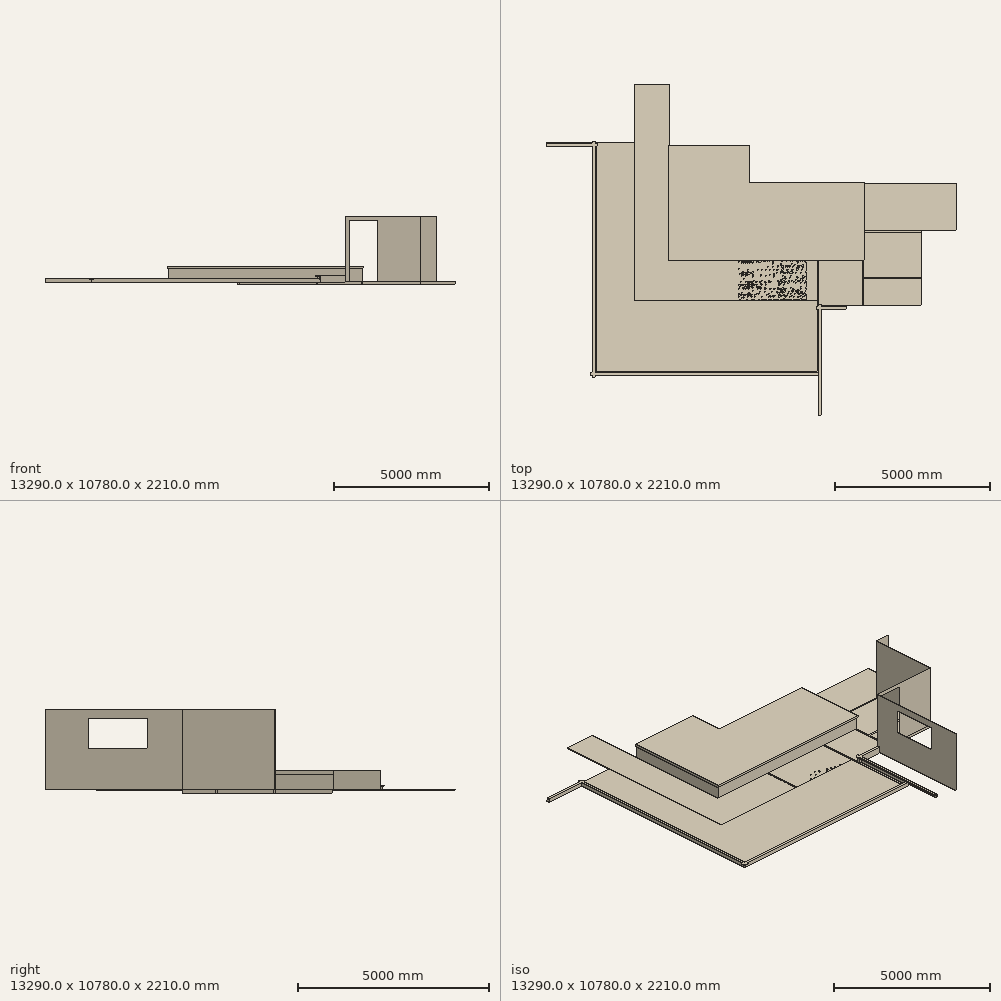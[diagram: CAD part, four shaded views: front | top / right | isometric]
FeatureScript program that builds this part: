
annotation { "Feature Type Name" : "Feature", "Feature Type Description" : "" }
export const myFeature = defineFeature(function(context is Context, id is Id, definition is map)
    precondition{}
    {
        {
            var Q0;
            Q0=qCreatedBy(makeId("Top.planeOp"),FACE);
            var sketch = newSketch(context, id + "F0", { "sketchPlane" : qUnion([Q0])});
            skLineSegment(sketch, "E0", {"start": v(0, 0) * mm, "end": v(0, 1220) * mm});
            skLineSegment(sketch, "E1", {"start": v(0, 1220) * mm, "end": v(-2595, 1220) * mm});
            skLineSegment(sketch, "E2", {"start": v(-2595, 1220) * mm, "end": v(-2595, -2530) * mm});
            skLineSegment(sketch, "E3", {"start": v(-2595, -2530) * mm, "end": v(3755, -2530) * mm});
            skLineSegment(sketch, "E4", {"start": v(3755, -2530) * mm, "end": v(3755, 0) * mm});
            skLineSegment(sketch, "E5", {"start": v(3755, 0) * mm, "end": v(0, 0) * mm});
            skSolve(sketch);
        }
        {
            var Q0;
            Q0 = qSketchRegion(id + "F0", true);
            extrude(context, id + "F1", {"entities" : qUnion([Q0]), "oppositeDirection" : true, "depth" : 85 * mm});
        }
        {
            var Q0;
            Q0=makeQuery(id+"F1.opExtrude","CAP_FACE",FACE,{"disambiguationData":[OSD([sQuery(id+"F0.wireOp",EDGE,"E0"),sQuery(id+"F0.wireOp",EDGE,"E1"),sQuery(id+"F0.wireOp",EDGE,"E2"),sQuery(id+"F0.wireOp",EDGE,"E3"),sQuery(id+"F0.wireOp",EDGE,"E4"),sQuery(id+"F0.wireOp",EDGE,"E5")])],"isStart":false});
            var sketch = newSketch(context, id + "F2", { "sketchPlane" : qUnion([Q0])});
            skLineSegment(sketch, "E6", {"start": v(-2565, -1220) * mm, "end": v(-2565, 2500) * mm});
            skLineSegment(sketch, "E7", {"start": v(-2565, 2500) * mm, "end": v(3725, 2500) * mm});
            skLineSegment(sketch, "E8", {"start": v(3725, 2500) * mm, "end": v(3725, 0) * mm});
            skLineSegment(sketch, "E9", {"start": v(3725, 0) * mm, "end": v(0, 0) * mm});
            skLineSegment(sketch, "E10", {"start": v(0, 0) * mm, "end": v(0, -1220) * mm});
            skLineSegment(sketch, "E11", {"start": v(0, -1220) * mm, "end": v(-2565, -1220) * mm});
            skSolve(sketch);
        }
        {
            var Q0;
            Q0 = qSketchRegion(id + "F2", true);
            extrude(context, id + "F3", {"entities" : qUnion([Q0]), "operationType" : NewBodyOperationType.ADD, "depth" : 410 * mm});
        }
        {
            var Q0;
            Q0=makeQuery(id+"F3.opExtrude","CAP_FACE",FACE,{"disambiguationData":[OSD([sQuery(id+"F2.wireOp",EDGE,"E6"),sQuery(id+"F2.wireOp",EDGE,"E7"),sQuery(id+"F2.wireOp",EDGE,"E8"),sQuery(id+"F2.wireOp",EDGE,"E9"),sQuery(id+"F2.wireOp",EDGE,"E10"),sQuery(id+"F2.wireOp",EDGE,"E11")])],"isStart":false});
            var sketch = newSketch(context, id + "F4", { "sketchPlane" : qUnion([Q0])});
            skLineSegment(sketch, "E12", {"start": v(-2565, 2500) * mm, "end": v(1875, 2500) * mm});
            skLineSegment(sketch, "E13", {"start": v(1875, 2500) * mm, "end": v(1875, 3800) * mm});
            skLineSegment(sketch, "E14", {"start": v(1875, 3800) * mm, "end": v(-3705, 3800) * mm});
            skLineSegment(sketch, "E15", {"start": v(-3705, 3800) * mm, "end": v(-3705, -3200) * mm});
            skLineSegment(sketch, "E16", {"start": v(-3705, -3200) * mm, "end": v(-2565, -3200) * mm});
            skLineSegment(sketch, "E17", {"start": v(-2565, -3200) * mm, "end": v(-2565, 2500) * mm});
            skSolve(sketch);
        }
        {
            var Q0;
            Q0 = qSketchRegion(id + "F4", true);
            extrude(context, id + "F5", {"entities" : qUnion([Q0]), "depth" : 25 * mm});
        }
        {
            var Q0;
            Q0=makeQuery(id+"F5.opExtrude","CAP_FACE",FACE,{"disambiguationData":[OSD([sQuery(id+"F4.wireOp",EDGE,"E12"),sQuery(id+"F4.wireOp",EDGE,"E13"),sQuery(id+"F4.wireOp",EDGE,"E14"),sQuery(id+"F4.wireOp",EDGE,"E15"),sQuery(id+"F4.wireOp",EDGE,"E16"),sQuery(id+"F4.wireOp",EDGE,"E17")])],"isStart":true});
            var sketch = newSketch(context, id + "F6", { "sketchPlane" : qUnion([Q0])});
            skLineSegment(sketch, "E18", {"start": v(2215, -3980) * mm, "end": v(3165, -3980) * mm});
            skLineSegment(sketch, "E19", {"start": v(2215, -3980) * mm, "end": v(2215, -6110) * mm});
            skLineSegment(sketch, "E20", {"start": v(2215, -6110) * mm, "end": v(-4960, -6110) * mm});
            skLineSegment(sketch, "E21", {"start": v(-4960, -6110) * mm, "end": v(-4960, 1295) * mm});
            skLineSegment(sketch, "E22", {"start": v(-4960, 1295) * mm, "end": v(-6565, 1295) * mm});
            skLineSegment(sketch, "E23", {"start": v(-6565, 1295) * mm, "end": v(-6565, 1170) * mm});
            skLineSegment(sketch, "E24", {"start": v(-6565, 1170) * mm, "end": v(-5085, 1170) * mm});
            skLineSegment(sketch, "E25", {"start": v(-5085, 1170) * mm, "end": v(-5085, -6235) * mm});
            skLineSegment(sketch, "E26", {"start": v(-5085, -6235) * mm, "end": v(2340, -6235) * mm});
            skLineSegment(sketch, "E27", {"start": v(2340, -6235) * mm, "end": v(2340, -4105) * mm});
            skLineSegment(sketch, "E28", {"start": v(2340, -4105) * mm, "end": v(3165, -4105) * mm});
            skLineSegment(sketch, "E29", {"start": v(3165, -4105) * mm, "end": v(3165, -3980) * mm});
            skSolve(sketch);
        }
        {
            var Q0;
            Q0=makeQuery(id+"F6.imprint","IMPRINT",FACE,{"disambiguationData":[TD([[makeQuery(id+"F6.imprint","IMPRINT",EDGE,{"derivedFrom":sQuery(id+"F6.wireOp",EDGE,"E18")}),-1.0]])]});
            extrude(context, id + "F7", {"entities" : qUnion([Q0]), "oppositeDirection" : true, "offsetDistance" : 25 * mm, "depth" : 25 * mm});
        }
        {
            var Q0;
            Q0=makeQuery(id+"F7.opExtrude","CAP_FACE",FACE,{"disambiguationData":[OSD([sQuery(id+"F6.wireOp",EDGE,"E18"),sQuery(id+"F6.wireOp",EDGE,"E19"),sQuery(id+"F6.wireOp",EDGE,"E20"),sQuery(id+"F6.wireOp",EDGE,"E21"),sQuery(id+"F6.wireOp",EDGE,"E22"),sQuery(id+"F6.wireOp",EDGE,"E23"),sQuery(id+"F6.wireOp",EDGE,"E24"),sQuery(id+"F6.wireOp",EDGE,"E25"),sQuery(id+"F6.wireOp",EDGE,"E26"),sQuery(id+"F6.wireOp",EDGE,"E27"),sQuery(id+"F6.wireOp",EDGE,"E28"),sQuery(id+"F6.wireOp",EDGE,"E29")])],"isStart":true});
            var sketch = newSketch(context, id + "F8", { "sketchPlane" : qUnion([Q0])});
            skLineSegment(sketch, "E30", {"start": v(3140, -4005) * mm, "end": v(3140, -4080) * mm});
            skLineSegment(sketch, "E31", {"start": v(3140, -4080) * mm, "end": v(2340, -4080) * mm});
            skLineSegment(sketch, "E32", {"start": v(2315, -4105) * mm, "end": v(2315, -6135) * mm});
            skLineSegment(sketch, "E33", {"start": v(2315, -6135) * mm, "end": v(2240, -6135) * mm});
            skLineSegment(sketch, "E34", {"start": v(2240, -6135) * mm, "end": v(2240, -6210) * mm});
            skLineSegment(sketch, "E35", {"start": v(2240, -6210) * mm, "end": v(508.75, -6210) * mm});
            skLineSegment(sketch, "E36", {"start": v(-4985, -6210) * mm, "end": v(-4985, -6135) * mm});
            skLineSegment(sketch, "E37", {"start": v(-4985, -6135) * mm, "end": v(-5060, -6135) * mm});
            skLineSegment(sketch, "E38", {"start": v(-5060, -6135) * mm, "end": v(-5060, -4383.75) * mm});
            skLineSegment(sketch, "E39", {"start": v(-5060, 1170) * mm, "end": v(-4985, 1170) * mm});
            skLineSegment(sketch, "E40", {"start": v(-4985, 1170) * mm, "end": v(-4985, 1270) * mm});
            skLineSegment(sketch, "E41", {"start": v(-4985, 1270) * mm, "end": v(-5085, 1270) * mm});
            skLineSegment(sketch, "E42", {"start": v(-5085, 1270) * mm, "end": v(-5085, 1195) * mm});
            skLineSegment(sketch, "E43", {"start": v(-5085, 1195) * mm, "end": v(-6540, 1195) * mm});
            skLineSegment(sketch, "E44", {"start": v(-6540, 1195) * mm, "end": v(-6540, 1270) * mm});
            skLineSegment(sketch, "E45", {"start": v(-6540, 1270) * mm, "end": v(-6565, 1270) * mm});
            skLineSegment(sketch, "E46", {"start": v(-6565, 1270) * mm, "end": v(-6565, 1170) * mm});
            skLineSegment(sketch, "E47", {"start": v(-6565, 1170) * mm, "end": v(-5085, 1170) * mm});
            skLineSegment(sketch, "E48", {"start": v(-5085, 1170) * mm, "end": v(-5085, -6235) * mm});
            skLineSegment(sketch, "E49", {"start": v(-5085, -6235) * mm, "end": v(2340, -6235) * mm});
            skLineSegment(sketch, "E50", {"start": v(2340, -6235) * mm, "end": v(2340, -4105) * mm});
            skLineSegment(sketch, "E51", {"start": v(2340, -4105) * mm, "end": v(3165, -4105) * mm});
            skLineSegment(sketch, "E52", {"start": v(3165, -4105) * mm, "end": v(3165, -4005) * mm});
            skLineSegment(sketch, "E53", {"start": v(3165, -4005) * mm, "end": v(3140, -4005) * mm});
            skLineSegment(sketch, "E54", {"start": v(2340, -4080) * mm, "end": v(2340, -4005) * mm});
            skLineSegment(sketch, "E55", {"start": v(2340, -4005) * mm, "end": v(2240, -4005) * mm});
            skLineSegment(sketch, "E56", {"start": v(2240, -4005) * mm, "end": v(2240, -4105) * mm});
            skLineSegment(sketch, "E57", {"start": v(2240, -4105) * mm, "end": v(2315, -4105) * mm});
            skLineSegment(sketch, "E58", {"start": v(-1422.5, -6210) * mm, "end": v(-1422.5, -6135) * mm});
            skLineSegment(sketch, "E59", {"start": v(-1422.5, -6135) * mm, "end": v(-1322.5, -6135) * mm});
            skLineSegment(sketch, "E60", {"start": v(-1322.5, -6135) * mm, "end": v(-1322.5, -6210) * mm});
            skLineSegment(sketch, "E61", {"start": v(-3253.75, -6210) * mm, "end": v(-3253.75, -6135) * mm});
            skLineSegment(sketch, "E62", {"start": v(-3253.75, -6135) * mm, "end": v(-3153.75, -6135) * mm});
            skLineSegment(sketch, "E63", {"start": v(-3153.75, -6135) * mm, "end": v(-3153.75, -6210) * mm});
            skLineSegment(sketch, "E64", {"start": v(408.75, -6210) * mm, "end": v(408.75, -6135) * mm});
            skLineSegment(sketch, "E65", {"start": v(408.75, -6135) * mm, "end": v(508.75, -6135) * mm});
            skLineSegment(sketch, "E66", {"start": v(508.75, -6135) * mm, "end": v(508.75, -6210) * mm});
            skLineSegment(sketch, "E67.trimOffspring", {"start": v(-3253.75, -6210) * mm, "end": v(-4985, -6210) * mm});
            skLineSegment(sketch, "E68.trimOffspring", {"start": v(-1422.5, -6210) * mm, "end": v(-3153.75, -6210) * mm});
            skLineSegment(sketch, "E69.trimOffspring", {"start": v(408.75, -6210) * mm, "end": v(-1322.5, -6210) * mm});
            skLineSegment(sketch, "E70", {"start": v(-5060, -4383.75) * mm, "end": v(-4985, -4383.75) * mm});
            skLineSegment(sketch, "E71", {"start": v(-4985, -4383.75) * mm, "end": v(-4985, -4283.75) * mm});
            skLineSegment(sketch, "E72", {"start": v(-4985, -4283.75) * mm, "end": v(-5060, -4283.75) * mm});
            skLineSegment(sketch, "E73", {"start": v(-5060, -2532.5) * mm, "end": v(-4985, -2532.5) * mm});
            skLineSegment(sketch, "E74", {"start": v(-4985, -2532.5) * mm, "end": v(-4985, -2432.5) * mm});
            skLineSegment(sketch, "E75", {"start": v(-4985, -2432.5) * mm, "end": v(-5060, -2432.5) * mm});
            skLineSegment(sketch, "E76", {"start": v(-5060, -681.25) * mm, "end": v(-4985, -681.25) * mm});
            skLineSegment(sketch, "E77", {"start": v(-4985, -681.25) * mm, "end": v(-4985, -581.25) * mm});
            skLineSegment(sketch, "E78", {"start": v(-4985, -581.25) * mm, "end": v(-5060, -581.25) * mm});
            skLineSegment(sketch, "E79.trimOffspring", {"start": v(-5060, -581.25) * mm, "end": v(-5060, 1170) * mm});
            skLineSegment(sketch, "E80.trimOffspring", {"start": v(-5060, -2432.5) * mm, "end": v(-5060, -681.25) * mm});
            skLineSegment(sketch, "E81.trimOffspring", {"start": v(-5060, -4283.75) * mm, "end": v(-5060, -2532.5) * mm});
            skSolve(sketch);
        }
        {
            var Q0;
            Q0 = qSketchRegion(id + "F8", true);
            extrude(context, id + "F9", {"entities" : qUnion([Q0]), "operationType" : NewBodyOperationType.ADD, "depth" : 75 * mm});
        }
        {
            var Q0;
            Q0=makeQuery(id+"F9.opExtrude","CAP_FACE",FACE,{"disambiguationData":[OSD([sQuery(id+"F8.wireOp",EDGE,"E30"),sQuery(id+"F8.wireOp",EDGE,"E31"),sQuery(id+"F8.wireOp",EDGE,"E32"),sQuery(id+"F8.wireOp",EDGE,"E33"),sQuery(id+"F8.wireOp",EDGE,"E34"),sQuery(id+"F8.wireOp",EDGE,"E35"),sQuery(id+"F8.wireOp",EDGE,"E36"),sQuery(id+"F8.wireOp",EDGE,"E37"),sQuery(id+"F8.wireOp",EDGE,"E38"),sQuery(id+"F8.wireOp",EDGE,"E39"),sQuery(id+"F8.wireOp",EDGE,"E40"),sQuery(id+"F8.wireOp",EDGE,"E41"),sQuery(id+"F8.wireOp",EDGE,"E42"),sQuery(id+"F8.wireOp",EDGE,"E43"),sQuery(id+"F8.wireOp",EDGE,"E44"),sQuery(id+"F8.wireOp",EDGE,"E45"),sQuery(id+"F8.wireOp",EDGE,"E46"),sQuery(id+"F8.wireOp",EDGE,"E47"),sQuery(id+"F8.wireOp",EDGE,"E48"),sQuery(id+"F8.wireOp",EDGE,"E49"),sQuery(id+"F8.wireOp",EDGE,"E50"),sQuery(id+"F8.wireOp",EDGE,"E51"),sQuery(id+"F8.wireOp",EDGE,"E52"),sQuery(id+"F8.wireOp",EDGE,"E53"),sQuery(id+"F8.wireOp",EDGE,"E54"),sQuery(id+"F8.wireOp",EDGE,"E55"),sQuery(id+"F8.wireOp",EDGE,"E56"),sQuery(id+"F8.wireOp",EDGE,"E57"),sQuery(id+"F8.wireOp",EDGE,"E58"),sQuery(id+"F8.wireOp",EDGE,"E59"),sQuery(id+"F8.wireOp",EDGE,"E60"),sQuery(id+"F8.wireOp",EDGE,"E61"),sQuery(id+"F8.wireOp",EDGE,"E62"),sQuery(id+"F8.wireOp",EDGE,"E63"),sQuery(id+"F8.wireOp",EDGE,"E64"),sQuery(id+"F8.wireOp",EDGE,"E65"),sQuery(id+"F8.wireOp",EDGE,"E66"),sQuery(id+"F8.wireOp",EDGE,"E67.trimOffspring"),sQuery(id+"F8.wireOp",EDGE,"E68.trimOffspring"),sQuery(id+"F8.wireOp",EDGE,"E69.trimOffspring"),sQuery(id+"F8.wireOp",EDGE,"E70"),sQuery(id+"F8.wireOp",EDGE,"E71"),sQuery(id+"F8.wireOp",EDGE,"E72"),sQuery(id+"F8.wireOp",EDGE,"E73"),sQuery(id+"F8.wireOp",EDGE,"E74"),sQuery(id+"F8.wireOp",EDGE,"E75"),sQuery(id+"F8.wireOp",EDGE,"E76"),sQuery(id+"F8.wireOp",EDGE,"E77"),sQuery(id+"F8.wireOp",EDGE,"E78"),sQuery(id+"F8.wireOp",EDGE,"E79.trimOffspring"),sQuery(id+"F8.wireOp",EDGE,"E80.trimOffspring"),sQuery(id+"F8.wireOp",EDGE,"E81.trimOffspring")])],"isStart":false});
            var sketch = newSketch(context, id + "F10", { "sketchPlane" : qUnion([Q0])});
            skLineSegment(sketch, "E82", {"start": v(3165, -4005) * mm, "end": v(3165, -4105) * mm});
            skLineSegment(sketch, "E83", {"start": v(3165, -4105) * mm, "end": v(2340, -4105) * mm});
            skLineSegment(sketch, "E84", {"start": v(2340, -4105) * mm, "end": v(2340, -7535) * mm});
            skLineSegment(sketch, "E85", {"start": v(2340, -7535) * mm, "end": v(2315, -7535) * mm});
            skLineSegment(sketch, "E86", {"start": v(2315, -7535) * mm, "end": v(2315, -4105) * mm});
            skLineSegment(sketch, "E87", {"start": v(2315, -4105) * mm, "end": v(2240, -4105) * mm});
            skLineSegment(sketch, "E88", {"start": v(2240, -4105) * mm, "end": v(2240, -4005) * mm});
            skLineSegment(sketch, "E89", {"start": v(2240, -4005) * mm, "end": v(2340, -4005) * mm});
            skLineSegment(sketch, "E90", {"start": v(2340, -4005) * mm, "end": v(2340, -4080) * mm});
            skLineSegment(sketch, "E91", {"start": v(2340, -4080) * mm, "end": v(3140, -4080) * mm});
            skLineSegment(sketch, "E92", {"start": v(3140, -4080) * mm, "end": v(3140, -4005) * mm});
            skLineSegment(sketch, "E93", {"start": v(3140, -4005) * mm, "end": v(3165, -4005) * mm});
            skSolve(sketch);
        }
        {
            var Q0;
            Q0=makeQuery(id+"F10.imprint","IMPRINT",FACE,{"disambiguationData":[TD([[makeQuery(id+"F10.imprint","IMPRINT",EDGE,{"derivedFrom":sQuery(id+"F10.wireOp",EDGE,"E82")}),1.0]])]});
            var Q1;
            {var subQ3=sQuery(id+"F10.wireOp",EDGE,"E85");Q1=makeQuery(id+"F10.imprint","IMPRINT",FACE,{"disambiguationData":[TD([[makeQuery(id+"F10.imprint","IMPRINT",EDGE,{"derivedFrom":subQ3}),-1.0]])]});}
            extrude(context, id + "F11", {"entities" : qUnion([Q0, Q1]), "operationType" : NewBodyOperationType.ADD, "depth" : 100 * mm});
        }
        {
            var Q0;
            Q0=makeQuery(id+"F11.opExtrude","CAP_FACE",FACE,{"disambiguationData":[OSD([sQuery(id+"F10.wireOp",EDGE,"E82"),sQuery(id+"F10.wireOp",EDGE,"E83"),sQuery(id+"F10.wireOp",EDGE,"E84"),sQuery(id+"F10.wireOp",EDGE,"E85"),sQuery(id+"F10.wireOp",EDGE,"E86"),sQuery(id+"F10.wireOp",EDGE,"E87"),sQuery(id+"F10.wireOp",EDGE,"E88"),sQuery(id+"F10.wireOp",EDGE,"E89"),sQuery(id+"F10.wireOp",EDGE,"E90"),sQuery(id+"F10.wireOp",EDGE,"E91"),sQuery(id+"F10.wireOp",EDGE,"E92"),sQuery(id+"F10.wireOp",EDGE,"E93")])],"isStart":false});
            var sketch = newSketch(context, id + "F12", { "sketchPlane" : qUnion([Q0])});
            skLineSegment(sketch, "E94", {"start": v(3165, -4105) * mm, "end": v(3165, -4005) * mm});
            skLineSegment(sketch, "E95", {"start": v(3165, -4005) * mm, "end": v(2340, -4005) * mm});
            skLineSegment(sketch, "E96", {"start": v(2180, -4005) * mm, "end": v(2180, -4105) * mm});
            skLineSegment(sketch, "E97", {"start": v(2180, -4105) * mm, "end": v(2240, -4105) * mm});
            skLineSegment(sketch, "E98", {"start": v(2240, -4105) * mm, "end": v(2240, -7535) * mm});
            skLineSegment(sketch, "E99", {"start": v(2240, -7535) * mm, "end": v(2340, -7535) * mm});
            skLineSegment(sketch, "E100", {"start": v(2340, -7535) * mm, "end": v(2340, -4105) * mm});
            skLineSegment(sketch, "E101", {"start": v(2340, -4105) * mm, "end": v(3165, -4105) * mm});
            skLineSegment(sketch, "E102", {"start": v(2240, -4005) * mm, "end": v(2240, -3945) * mm});
            skLineSegment(sketch, "E103", {"start": v(2240, -3945) * mm, "end": v(2340, -3945) * mm});
            skLineSegment(sketch, "E104", {"start": v(2340, -3945) * mm, "end": v(2340, -4005) * mm});
            skLineSegment(sketch, "E105.trimOffspring", {"start": v(2240, -4005) * mm, "end": v(2180, -4005) * mm});
            skSolve(sketch);
        }
        {
            var Q0;
            {var subQ1=sQuery(id+"F12.wireOp",EDGE,"E94");Q0=makeQuery(id+"F12.imprint","IMPRINT",FACE,{"disambiguationData":[TD([[makeQuery(id+"F12.imprint","IMPRINT",EDGE,{"derivedFrom":subQ1}),1.0]])]});}
            var Q1;
            Q1=makeQuery(id+"F12.imprint","IMPRINT",FACE,{"disambiguationData":[TD([[makeQuery(id+"F12.imprint","IMPRINT",EDGE,{"derivedFrom":sQuery(id+"F12.wireOp",EDGE,"E96")}),1.0]])]});
            var Q2;
            Q2=makeQuery(id+"F12.imprint","IMPRINT",FACE,{"disambiguationData":[TD([[makeQuery(id+"F12.imprint","IMPRINT",EDGE,{"derivedFrom":sQuery(id+"F12.wireOp",EDGE,"E102")}),-1.0]])]});
            var Q3;
            {var subQ0=sQuery(id+"F12.wireOp",EDGE,"E98");Q3=makeQuery(id+"F12.imprint","IMPRINT",FACE,{"disambiguationData":[TD([[makeQuery(id+"F12.imprint","IMPRINT",EDGE,{"derivedFrom":subQ0}),1.0]])]});}
            var Q4;
            {var subQ2=makeQuery(id+"F11.opExtrude","CAP_EDGE",EDGE,{"disambiguationData":[OSD([sQuery(id+"F10.wireOp",EDGE,"E90")])],"isStart":false});Q4=makeQuery(id+"F12.imprint","IMPRINT",FACE,{"disambiguationData":[TD([[makeQuery(id+"F12.imprint","IMPRINT",EDGE,{"derivedFrom":subQ2}),-1.0]])]});}
            extrude(context, id + "F13", {"entities" : qUnion([Q0, Q1, Q2, Q3, Q4]), "operationType" : NewBodyOperationType.ADD, "depth" : 25 * mm});
        }
        {
            var Q0;
            Q0=makeQuery(id+"F9.opExtrude","CAP_FACE",FACE,{"disambiguationData":[OSD([sQuery(id+"F8.wireOp",EDGE,"E30"),sQuery(id+"F8.wireOp",EDGE,"E31"),sQuery(id+"F8.wireOp",EDGE,"E32"),sQuery(id+"F8.wireOp",EDGE,"E33"),sQuery(id+"F8.wireOp",EDGE,"E34"),sQuery(id+"F8.wireOp",EDGE,"E35"),sQuery(id+"F8.wireOp",EDGE,"E36"),sQuery(id+"F8.wireOp",EDGE,"E37"),sQuery(id+"F8.wireOp",EDGE,"E38"),sQuery(id+"F8.wireOp",EDGE,"E39"),sQuery(id+"F8.wireOp",EDGE,"E40"),sQuery(id+"F8.wireOp",EDGE,"E41"),sQuery(id+"F8.wireOp",EDGE,"E42"),sQuery(id+"F8.wireOp",EDGE,"E43"),sQuery(id+"F8.wireOp",EDGE,"E44"),sQuery(id+"F8.wireOp",EDGE,"E45"),sQuery(id+"F8.wireOp",EDGE,"E46"),sQuery(id+"F8.wireOp",EDGE,"E47"),sQuery(id+"F8.wireOp",EDGE,"E48"),sQuery(id+"F8.wireOp",EDGE,"E49"),sQuery(id+"F8.wireOp",EDGE,"E50"),sQuery(id+"F8.wireOp",EDGE,"E51"),sQuery(id+"F8.wireOp",EDGE,"E52"),sQuery(id+"F8.wireOp",EDGE,"E53"),sQuery(id+"F8.wireOp",EDGE,"E54"),sQuery(id+"F8.wireOp",EDGE,"E55"),sQuery(id+"F8.wireOp",EDGE,"E56"),sQuery(id+"F8.wireOp",EDGE,"E57"),sQuery(id+"F8.wireOp",EDGE,"E58"),sQuery(id+"F8.wireOp",EDGE,"E59"),sQuery(id+"F8.wireOp",EDGE,"E60"),sQuery(id+"F8.wireOp",EDGE,"E61"),sQuery(id+"F8.wireOp",EDGE,"E62"),sQuery(id+"F8.wireOp",EDGE,"E63"),sQuery(id+"F8.wireOp",EDGE,"E64"),sQuery(id+"F8.wireOp",EDGE,"E65"),sQuery(id+"F8.wireOp",EDGE,"E66"),sQuery(id+"F8.wireOp",EDGE,"E67.trimOffspring"),sQuery(id+"F8.wireOp",EDGE,"E68.trimOffspring"),sQuery(id+"F8.wireOp",EDGE,"E69.trimOffspring"),sQuery(id+"F8.wireOp",EDGE,"E70"),sQuery(id+"F8.wireOp",EDGE,"E71"),sQuery(id+"F8.wireOp",EDGE,"E72"),sQuery(id+"F8.wireOp",EDGE,"E73"),sQuery(id+"F8.wireOp",EDGE,"E74"),sQuery(id+"F8.wireOp",EDGE,"E75"),sQuery(id+"F8.wireOp",EDGE,"E76"),sQuery(id+"F8.wireOp",EDGE,"E77"),sQuery(id+"F8.wireOp",EDGE,"E78"),sQuery(id+"F8.wireOp",EDGE,"E79.trimOffspring"),sQuery(id+"F8.wireOp",EDGE,"E80.trimOffspring"),sQuery(id+"F8.wireOp",EDGE,"E81.trimOffspring")])],"isStart":false});
            var sketch = newSketch(context, id + "F14", { "sketchPlane" : qUnion([Q0])});
            skLineSegment(sketch, "E106", {"start": v(2315, -6135) * mm, "end": v(2315, -6235) * mm});
            skLineSegment(sketch, "E107", {"start": v(2315, -6235) * mm, "end": v(-4985, -6235) * mm});
            skLineSegment(sketch, "E108", {"start": v(-5145, -6235) * mm, "end": v(-5145, -6135) * mm});
            skLineSegment(sketch, "E109", {"start": v(-5145, -6135) * mm, "end": v(-5085, -6135) * mm});
            skLineSegment(sketch, "E110", {"start": v(-5085, -6135) * mm, "end": v(-5085, 1170) * mm});
            skLineSegment(sketch, "E111", {"start": v(-5085, 1170) * mm, "end": v(-6565, 1170) * mm});
            skLineSegment(sketch, "E112", {"start": v(-6565, 1170) * mm, "end": v(-6565, 1270) * mm});
            skLineSegment(sketch, "E113", {"start": v(-6565, 1270) * mm, "end": v(-5085, 1270) * mm});
            skLineSegment(sketch, "E114", {"start": v(-5085, 1270) * mm, "end": v(-5085, 1330) * mm});
            skLineSegment(sketch, "E115", {"start": v(-5085, 1330) * mm, "end": v(-4985, 1330) * mm});
            skLineSegment(sketch, "E116", {"start": v(-4985, 1330) * mm, "end": v(-4985, 1270) * mm});
            skLineSegment(sketch, "E117", {"start": v(-4985, 1270) * mm, "end": v(-4925, 1270) * mm});
            skLineSegment(sketch, "E118", {"start": v(-4925, 1270) * mm, "end": v(-4925, 1170) * mm});
            skLineSegment(sketch, "E119", {"start": v(-4925, 1170) * mm, "end": v(-4985, 1170) * mm});
            skLineSegment(sketch, "E120", {"start": v(-4985, 1170) * mm, "end": v(-4985, -6135) * mm});
            skLineSegment(sketch, "E121", {"start": v(-4985, -6135) * mm, "end": v(2315, -6135) * mm});
            skLineSegment(sketch, "E122", {"start": v(-4985, -6235) * mm, "end": v(-4985, -6295) * mm});
            skLineSegment(sketch, "E123", {"start": v(-4985, -6295) * mm, "end": v(-5085, -6295) * mm});
            skLineSegment(sketch, "E124", {"start": v(-5085, -6295) * mm, "end": v(-5085, -6235) * mm});
            skLineSegment(sketch, "E125.trimOffspring", {"start": v(-5085, -6235) * mm, "end": v(-5145, -6235) * mm});
            skSolve(sketch);
        }
        {
            var Q0;
            Q0 = qSketchRegion(id + "F14", true);
            extrude(context, id + "F15", {"entities" : qUnion([Q0]), "operationType" : NewBodyOperationType.ADD, "depth" : 25 * mm});
        }
        {
            var Q0;
            Q0=makeQuery(id+"F13.opExtrude","CAP_EDGE",EDGE,{"disambiguationData":[OSD([sQuery(id+"F12.wireOp",EDGE,"E96")])],"isStart":true});
            var Q1;
            Q1=makeQuery(id+"F13.opExtrude","CAP_EDGE",EDGE,{"disambiguationData":[OSD([sQuery(id+"F12.wireOp",EDGE,"E103")])],"isStart":true});
            var Q2;
            Q2=makeQuery(id+"F15.opExtrude","CAP_EDGE",EDGE,{"disambiguationData":[OSD([sQuery(id+"F14.wireOp",EDGE,"E123")])],"isStart":true});
            var Q3;
            Q3=makeQuery(id+"F15.opExtrude","CAP_EDGE",EDGE,{"disambiguationData":[OSD([sQuery(id+"F14.wireOp",EDGE,"E108")])],"isStart":true});
            var Q4;
            Q4=makeQuery(id+"F15.opExtrude","CAP_EDGE",EDGE,{"disambiguationData":[OSD([sQuery(id+"F14.wireOp",EDGE,"E115")])],"isStart":true});
            var Q5;
            Q5=makeQuery(id+"F15.opExtrude","CAP_EDGE",EDGE,{"disambiguationData":[OSD([sQuery(id+"F14.wireOp",EDGE,"E118")])],"isStart":true});
            chamfer(context, id + "F16", {"entities" : qUnion([Q0, Q1, Q2, Q3, Q4, Q5]), "width" : 25 * mm, "tangentPropagation" : true});
        }
        {
            var Q0;
            Q0=makeQuery(id+"F5.opExtrude","CAP_FACE",FACE,{"disambiguationData":[OSD([sQuery(id+"F4.wireOp",EDGE,"E12"),sQuery(id+"F4.wireOp",EDGE,"E13"),sQuery(id+"F4.wireOp",EDGE,"E14"),sQuery(id+"F4.wireOp",EDGE,"E15"),sQuery(id+"F4.wireOp",EDGE,"E16"),sQuery(id+"F4.wireOp",EDGE,"E17")])],"isStart":true});
            var sketch = newSketch(context, id + "F17", { "sketchPlane" : qUnion([Q0])});
            skLineSegment(sketch, "E126", {"start": v(-3705, 1295) * mm, "end": v(-4960, 1295) * mm});
            skLineSegment(sketch, "E127", {"start": v(-4960, 1295) * mm, "end": v(-4960, -6110) * mm});
            skLineSegment(sketch, "E128", {"start": v(-4960, -6110) * mm, "end": v(2215, -6110) * mm});
            skLineSegment(sketch, "E129", {"start": v(2215, -6110) * mm, "end": v(2215, -3800) * mm});
            skLineSegment(sketch, "E130", {"start": v(2215, -3800) * mm, "end": v(1875, -3800) * mm});
            skLineSegment(sketch, "E131", {"start": v(1875, -3800) * mm, "end": v(-3705, -3800) * mm});
            skLineSegment(sketch, "E132", {"start": v(-3705, -3800) * mm, "end": v(-3705, 1295) * mm});
            skSolve(sketch);
        }
        {
            var Q0;
            Q0 = qSketchRegion(id + "F17", true);
            extrude(context, id + "F18", {"entities" : qUnion([Q0]), "oppositeDirection" : true, "depth" : 25 * mm});
        }
        {
            var Q0;
            Q0=makeQuery(id+"F5.opExtrude","CAP_FACE",FACE,{"disambiguationData":[OSD([sQuery(id+"F4.wireOp",EDGE,"E12"),sQuery(id+"F4.wireOp",EDGE,"E13"),sQuery(id+"F4.wireOp",EDGE,"E14"),sQuery(id+"F4.wireOp",EDGE,"E15"),sQuery(id+"F4.wireOp",EDGE,"E16"),sQuery(id+"F4.wireOp",EDGE,"E17")])],"isStart":true});
            var sketch = newSketch(context, id + "F19", { "sketchPlane" : qUnion([Q0])});
            skLineSegment(sketch, "E133", {"start": v(3165, -7580) * mm, "end": v(3165, -3980) * mm});
            skLineSegment(sketch, "E134", {"start": v(3165, -3980) * mm, "end": v(5575, -3980) * mm});
            skLineSegment(sketch, "E135", {"start": v(5575, -3980) * mm, "end": v(5575, -1545) * mm});
            skLineSegment(sketch, "E136", {"start": v(5575, -1545) * mm, "end": v(6110, -1545) * mm});
            skLineSegment(sketch, "E137", {"start": v(6110, -1545) * mm, "end": v(6110, -1550) * mm});
            skLineSegment(sketch, "E138", {"start": v(6110, -1550) * mm, "end": v(5580, -1550) * mm});
            skLineSegment(sketch, "E139", {"start": v(5580, -1550) * mm, "end": v(5580, -3985) * mm});
            skLineSegment(sketch, "E140", {"start": v(5580, -3985) * mm, "end": v(3170, -3985) * mm});
            skLineSegment(sketch, "E141", {"start": v(3170, -3985) * mm, "end": v(3170, -7580) * mm});
            skLineSegment(sketch, "E142", {"start": v(3170, -7580) * mm, "end": v(3165, -7580) * mm});
            skSolve(sketch);
        }
        {
            var Q0;
            Q0 = qSketchRegion(id + "F19", true);
            extrude(context, id + "F20", {"entities" : qUnion([Q0]), "depth" : 2110 * mm});
        }
        {
            var Q0;
            Q0=makeQuery(id+"F3.opExtrude","CAP_FACE",FACE,{"disambiguationData":[OSD([sQuery(id+"F2.wireOp",EDGE,"E6"),sQuery(id+"F2.wireOp",EDGE,"E7"),sQuery(id+"F2.wireOp",EDGE,"E8"),sQuery(id+"F2.wireOp",EDGE,"E9"),sQuery(id+"F2.wireOp",EDGE,"E10"),sQuery(id+"F2.wireOp",EDGE,"E11")])],"isStart":false});
            var sketch = newSketch(context, id + "F21", { "sketchPlane" : qUnion([Q0])});
            skLineSegment(sketch, "E143", {"start": v(3725, 1545) * mm, "end": v(6725, 1545) * mm});
            skLineSegment(sketch, "E144", {"start": v(6725, 1545) * mm, "end": v(6725, 25) * mm});
            skLineSegment(sketch, "E145", {"start": v(6725, 25) * mm, "end": v(3725, 25) * mm});
            skLineSegment(sketch, "E146", {"start": v(3725, 25) * mm, "end": v(3725, 1545) * mm});
            skSolve(sketch);
        }
        {
            var Q0;
            Q0 = qSketchRegion(id + "F21", true);
            extrude(context, id + "F22", {"entities" : qUnion([Q0]), "depth" : 100 * mm, "offsetDistance" : 25 * mm});
        }
        {
            var Q0;
            Q0=makeQuery(id+"F7.opExtrude","CAP_FACE",FACE,{"disambiguationData":[OSD([sQuery(id+"F6.wireOp",EDGE,"E18"),sQuery(id+"F6.wireOp",EDGE,"E19"),sQuery(id+"F6.wireOp",EDGE,"E20"),sQuery(id+"F6.wireOp",EDGE,"E21"),sQuery(id+"F6.wireOp",EDGE,"E22"),sQuery(id+"F6.wireOp",EDGE,"E23"),sQuery(id+"F6.wireOp",EDGE,"E24"),sQuery(id+"F6.wireOp",EDGE,"E25"),sQuery(id+"F6.wireOp",EDGE,"E26"),sQuery(id+"F6.wireOp",EDGE,"E27"),sQuery(id+"F6.wireOp",EDGE,"E28"),sQuery(id+"F6.wireOp",EDGE,"E29")])],"isStart":true});
            var sketch = newSketch(context, id + "F23", { "sketchPlane" : qUnion([Q0])});
            skLineSegment(sketch, "E147", {"start": v(2215, -3980) * mm, "end": v(2215, -2500) * mm});
            skLineSegment(sketch, "E148", {"start": v(2215, -2500) * mm, "end": v(2265, -2500) * mm});
            skLineSegment(sketch, "E149", {"start": v(2265, -2500) * mm, "end": v(2265, -3980) * mm});
            skLineSegment(sketch, "E150", {"start": v(2265, -3980) * mm, "end": v(2215, -3980) * mm});
            skLineSegment(sketch, "E151", {"start": v(3725, -1545) * mm, "end": v(5575, -1545) * mm});
            skLineSegment(sketch, "E152", {"start": v(5575, -1545) * mm, "end": v(5575, -1595) * mm});
            skLineSegment(sketch, "E153", {"start": v(5575, -1595) * mm, "end": v(3725, -1595) * mm});
            skLineSegment(sketch, "E154", {"start": v(3725, -1595) * mm, "end": v(3725, -1545) * mm});
            skLineSegment(sketch, "E155", {"start": v(3725, -2500) * mm, "end": v(3675, -2500) * mm});
            skLineSegment(sketch, "E156", {"start": v(3675, -2500) * mm, "end": v(3675, -3980) * mm});
            skLineSegment(sketch, "E157", {"start": v(3675, -3980) * mm, "end": v(3725, -3980) * mm});
            skLineSegment(sketch, "E158", {"start": v(3725, -3980) * mm, "end": v(3725, -2500) * mm});
            skLineSegment(sketch, "E159", {"start": v(3725, -3050) * mm, "end": v(5575, -3050) * mm});
            skLineSegment(sketch, "E160", {"start": v(5575, -3050) * mm, "end": v(5575, -3100) * mm});
            skLineSegment(sketch, "E161", {"start": v(5575, -3100) * mm, "end": v(3725, -3100) * mm});
            skLineSegment(sketch, "E162", {"start": v(3725, -3100) * mm, "end": v(3725, -3050) * mm});
            skLineSegment(sketch, "E163", {"start": v(-285, -2500) * mm, "end": v(-285, -3800) * mm});
            skLineSegment(sketch, "E164", {"start": v(-285, -3800) * mm, "end": v(-335, -3800) * mm});
            skLineSegment(sketch, "E165", {"start": v(-335, -3800) * mm, "end": v(-335, -2500) * mm});
            skLineSegment(sketch, "E166", {"start": v(-335, -2500) * mm, "end": v(-285, -2500) * mm});
            skSolve(sketch);
        }
        {
            var Q0;
            Q0 = qSketchRegion(id + "F23", true);
            extrude(context, id + "F24", {"entities" : qUnion([Q0]), "oppositeDirection" : true, "depth" : 100 * mm, "offsetDistance" : 25 * mm});
        }
        {
            var Q0;
            Q0=makeQuery(id+"F24.opExtrude","CAP_FACE",FACE,{"disambiguationData":[OSD([sQuery(id+"F23.wireOp",EDGE,"E155"),sQuery(id+"F23.wireOp",EDGE,"E156"),sQuery(id+"F23.wireOp",EDGE,"E157"),sQuery(id+"F23.wireOp",EDGE,"E158"),sQuery(id+"F23.wireOp",EDGE,"E159"),sQuery(id+"F23.wireOp",EDGE,"E160"),sQuery(id+"F23.wireOp",EDGE,"E161")])],"isStart":true});
            var sketch = newSketch(context, id + "F25", { "sketchPlane" : qUnion([Q0])});
            skLineSegment(sketch, "E167", {"start": v(3725, -3050) * mm, "end": v(3725, -1595) * mm});
            skLineSegment(sketch, "E168", {"start": v(3725, -1595) * mm, "end": v(5575, -1595) * mm});
            skLineSegment(sketch, "E169", {"start": v(5575, -1595) * mm, "end": v(5575, -3050) * mm});
            skLineSegment(sketch, "E170", {"start": v(5575, -3050) * mm, "end": v(3725, -3050) * mm});
            skLineSegment(sketch, "E171", {"start": v(5575, -3100) * mm, "end": v(3725, -3100) * mm});
            skLineSegment(sketch, "E172", {"start": v(3725, -3100) * mm, "end": v(3725, -3980) * mm});
            skLineSegment(sketch, "E173", {"start": v(3725, -3980) * mm, "end": v(5575, -3980) * mm});
            skLineSegment(sketch, "E174", {"start": v(5575, -3980) * mm, "end": v(5575, -3100) * mm});
            skLineSegment(sketch, "E175", {"start": v(3675, -3980) * mm, "end": v(3675, -2500) * mm});
            skLineSegment(sketch, "E176", {"start": v(3675, -2500) * mm, "end": v(2265, -2500) * mm});
            skLineSegment(sketch, "E177", {"start": v(2265, -2500) * mm, "end": v(2265, -3980) * mm});
            skLineSegment(sketch, "E178", {"start": v(2265, -3980) * mm, "end": v(3675, -3980) * mm});
            skLineSegment(sketch, "E179.bottom", {"start": v(2215, -2500) * mm, "end": v(-285, -2500) * mm});
            skLineSegment(sketch, "E179.top", {"start": v(2215, -3800) * mm, "end": v(-285, -3800) * mm});
            skLineSegment(sketch, "E179.left", {"start": v(2215, -2500) * mm, "end": v(2215, -3800) * mm});
            skLineSegment(sketch, "E180", {"start": v(-285, -2500) * mm, "end": v(-285, -3800) * mm});
            skSolve(sketch);
        }
        {
            var Q0;
            Q0 = qSketchRegion(id + "F25", true);
            extrude(context, id + "F26", {"entities" : qUnion([Q0]), "oppositeDirection" : true, "depth" : 100 * mm, "offsetDistance" : 25 * mm});
        }
        {
            var Q0;
            Q0=makeQuery(id+"F20.opExtrude","SWEPT_FACE",FACE,{"disambiguationData":[OSD([sQuery(id+"F19.wireOp",EDGE,"E134")])]});
            var sketch = newSketch(context, id + "F27", { "sketchPlane" : qUnion([Q0])});
            skLineSegment(sketch, "E181.bottom", {"start": v(-4185, -495) * mm, "end": v(-3275, -495) * mm});
            skLineSegment(sketch, "E181.top", {"start": v(-4185, 1485) * mm, "end": v(-3275, 1485) * mm});
            skLineSegment(sketch, "E181.left", {"start": v(-4185, -495) * mm, "end": v(-4185, 1485) * mm});
            skLineSegment(sketch, "E181.right", {"start": v(-3275, -495) * mm, "end": v(-3275, 1485) * mm});
            skSolve(sketch);
        }
        {
            var Q0;
            Q0 = qSketchRegion(id + "F27", true);
            extrude(context, id + "F28", {"entities" : qUnion([Q0]), "operationType" : NewBodyOperationType.REMOVE, "endBound" : BoundingType.UP_TO_NEXT, "oppositeDirection" : true, "depth" : 25 * mm, "offsetDistance" : 25 * mm});
        }
        {
            var Q0;
            Q0=makeQuery(id+"F20.opExtrude","SWEPT_FACE",FACE,{"disambiguationData":[OSD([sQuery(id+"F19.wireOp",EDGE,"E133")])]});
            var sketch = newSketch(context, id + "F29", { "sketchPlane" : qUnion([Q0])});
            skLineSegment(sketch, "E182.bottom", {"start": v(4890, 1375) * mm, "end": v(6450, 1375) * mm});
            skLineSegment(sketch, "E182.top", {"start": v(4890, 585) * mm, "end": v(6450, 585) * mm});
            skLineSegment(sketch, "E182.left", {"start": v(4890, 1375) * mm, "end": v(4890, 585) * mm});
            skLineSegment(sketch, "E182.right", {"start": v(6450, 1375) * mm, "end": v(6450, 585) * mm});
            skSolve(sketch);
        }
        {
            var Q0;
            Q0 = qSketchRegion(id + "F29", true);
            extrude(context, id + "F30", {"entities" : qUnion([Q0]), "operationType" : NewBodyOperationType.REMOVE, "endBound" : BoundingType.UP_TO_NEXT, "oppositeDirection" : true, "depth" : 25 * mm, "offsetDistance" : 25 * mm});
        }
    });
